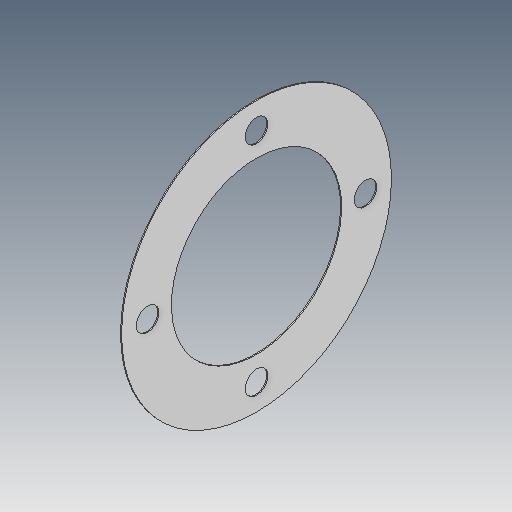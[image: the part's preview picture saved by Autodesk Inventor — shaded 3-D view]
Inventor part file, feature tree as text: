
AUTODESK INVENTOR PART (.ipt)
format: ipt  version: 2025 (Build 290162000, 162)  size: 305,664 bytes
history: native  units: in
note: dims shown in document units (in); Inventor stores cm internally (conversion verified against a paired STEP export)
features: sketch x2, extrude x1
ambient origin geometry x8: Origin, YZ Plane, XZ Plane, XY Plane, X Axis, Y Axis, Z Axis, Center Point
bodies: 实体1 (feature_tree)
feature tree (3):
  extrude  "拉伸1"  Depth=3.2283in
  sketch  "草图1"  dims[d0=0.4331in d2=3.2283in]
  sketch  "草图 - 环形阵列1"  dims[d1=5.1181in d3=3.2283in d4=0.4331in d5=2.0669in d6=1.5748in d8=360.0deg d10=0.0197in d11=0.0in]
